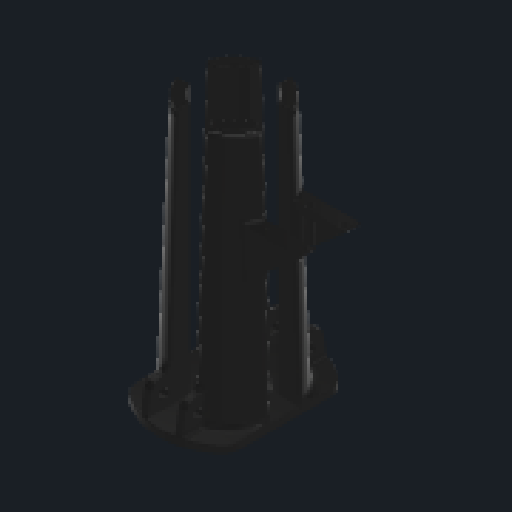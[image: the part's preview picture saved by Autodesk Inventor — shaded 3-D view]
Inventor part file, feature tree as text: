
AUTODESK INVENTOR PART (.ipt)
format: ipt  version: 2023 (Build 270158000, 158)  size: 1,583,104 bytes
history: native  units: mm
features: fillet x12, sketch x8, extrude x6, mirror x4, hole x4, draft x3, plane x3, projected_geometry x3, revolve x1, chamfer x1
ambient origin geometry x8: Origin, YZ Plane, XZ Plane, XY Plane, X Axis, Y Axis, Z Axis, Center Point
bodies: Solid1 (feature_tree)
feature tree (45):
  extrude  "Extrusion1"  Depth=35.75mm
  extrude  "Extrusion2"  Depth=80.0mm
  extrude  "Extrusion3"  Depth=27.5mm
  draft  "FaceDraft1"
  fillet  "Fillet1"  Radius=4.0mm
  fillet  "Fillet2"  Radius=27.8mm
  fillet  "Fillet3"  Radius=4.0mm
  plane  "Work Plane1"
  sketch  "Sketch5"  dims[d17=0.349066mm d18=4.0mm]
  revolve  "Revolution1"  [1 undecoded]
  extrude  "Extrusion4"  Depth=10.0mm
  extrude  "Extrusion5"  TaperAngle=45.0deg  [1 undecoded]
  draft  "FaceDraft2"
  mirror  "Mirror1"
  mirror  "Mirror2"
  fillet  "Fillet5"  [1 undecoded]
  fillet  "Fillet6"  [1 undecoded]
  fillet  "Fillet8"  Radius=24.7mm
  fillet  "Fillet9"  Radius=23.2mm
  chamfer  "Chamfer1"  Distance=11.0mm
  plane  "Work Plane2"
  extrude  "Extrusion6"  Depth=0.5mm TaperAngle=0.0deg
  draft  "FaceDraft4"
  plane  "Work Plane3"
  sketch  "Sketch12"  dims[d29=13.2mm d32=11.0mm d33=15.2mm d34=0.0mm d35=15.2mm d36=4.65mm d37=6.6mm d38=7.3mm d39=0.0mm d40=0.0mm d41=1.396263mm d43=5.5mm d44=2.0mm d46=0.5mm d47=1.0mm d48=0.3mm d49=2.0mm d50=45.0deg d51=-96.8mm d54=27.94mm d55=51.673462mm d56=30.94mm d57=2.98mm d58=3.225mm d60=30.265mm d62=18.0mm d65=30.94mm d66=0.0mm d70=15.54mm d75=8.726646mm d76=4.0mm d77=3.1mm d78=6.0mm d79=6.0mm d80=10.0mm d81=90.0deg d82=8.0mm d83=20.594885mm d84=6.5mm d85=6.0mm d86=5.5mm d87=10.0mm d88=90.0deg d89=8.0mm d90=20.594885mm d91=3.1mm d92=6.0mm d93=6.0mm d94=10.0mm d95=90.0deg d96=8.0mm d97=20.594885mm d98=6.5mm d99=6.0mm d100=5.5mm d101=10.0mm d102=90.0deg d103=30.0mm d104=90.0deg d105=2.0mm d107=2.0mm d108=2.0mm d109=1.75mm d110=0.7mm d111=0.5mm]
  hole  "Hole1"  [1 undecoded]
  hole  "Hole2"  [1 undecoded]
  mirror  "Mirror3"
  hole  "Hole3"  [1 undecoded]
  hole  "Hole4"  [1 undecoded]
  mirror  "Mirror4"
  fillet  "Fillet12"  [1 undecoded]
  fillet  "Fillet14"  Radius=1.396263mm
  fillet  "Fillet15"  Radius=5.5mm
  fillet  "Fillet16"  Radius=2.0mm
  fillet  "Fillet17"  Radius=0.5mm
  sketch  "Sketch1"  dims[d0=7.5mm d1=7.0mm d2=7.5mm d3=0.0mm d4=7.0mm d5=28.73603mm d6=35.75mm]
  sketch  "Sketch2"  dims[d7=135.0mm d8=0.0mm d9=80.0mm]
  sketch  "Sketch3"  dims[d10=55.0mm d11=27.5mm d12=4.0mm d13=0.0mm d14=27.8mm d15=4.0mm d16=0.0mm]
  sketch  "Sketch6"  dims[d19=10.0mm d20=1.2mm]
  sketch  "Sketch8"  dims[d21=-3.0mm d22=45.0deg d23=45.0deg d25=90.0deg d26=24.7mm d27=23.2mm]
  projected_geometry  "Projected Loop1"
  sketch  "Sketch9"  dims[d28=0.0mm]
  projected_geometry  "Projected Loop4"
  projected_geometry  "Projected Loop5"
note: 9 required parameter values undecoded (feature->parameter linkage not recoverable at this tier; creation-order binding heuristic only, values carry confidence <= 0.55)